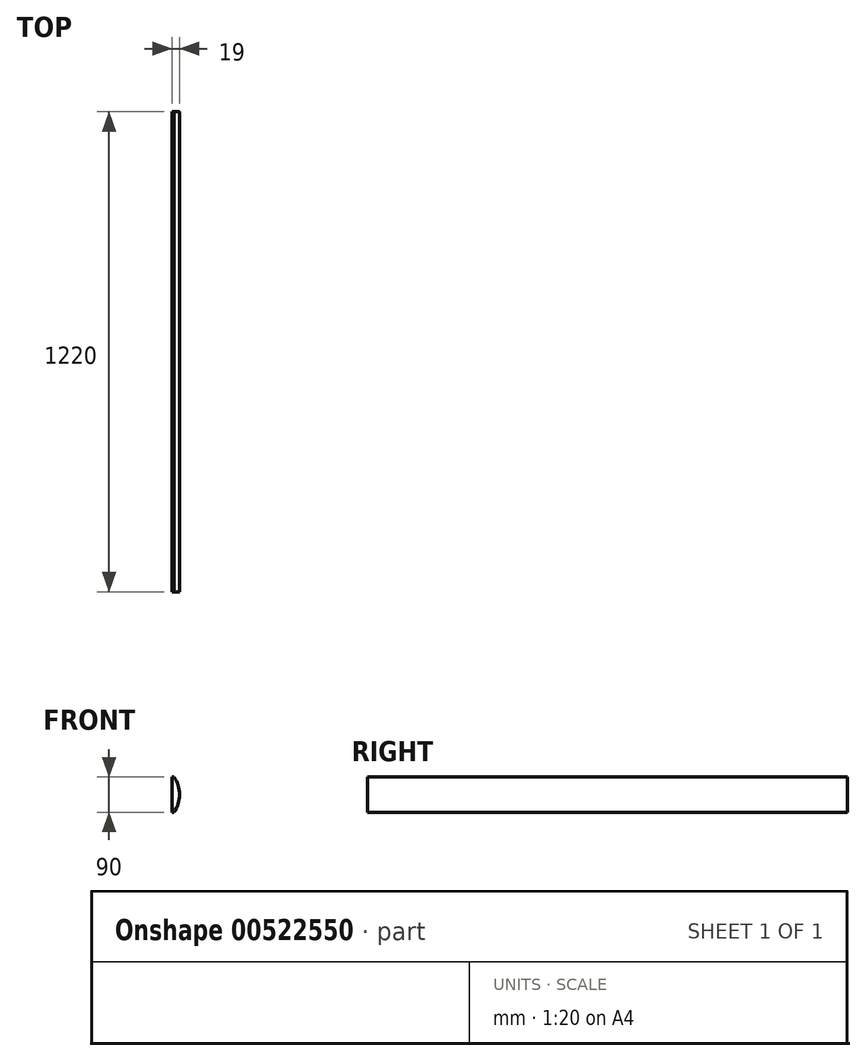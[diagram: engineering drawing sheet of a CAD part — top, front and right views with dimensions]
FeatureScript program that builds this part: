
annotation { "Feature Type Name" : "Feature", "Feature Type Description" : "" }
export const myFeature = defineFeature(function(context is Context, id is Id, definition is map)
    precondition{}
    {
        {
            var Q0;
            Q0=qCreatedBy(makeId("Front.planeOp"),FACE);
            var sketch = newSketch(context, id + "F0", { "sketchPlane" : qUnion([Q0])});
            skLineSegment(sketch, "E0", {"start": v(0, 0) * mm, "end": v(0, 90) * mm});
            skLineSegment(sketch, "E1", {"start": v(0, 0) * mm, "end": v(5, 0) * mm});
            skLineSegment(sketch, "E2", {"start": v(0, 90) * mm, "end": v(5, 90) * mm});
            skLineSegment(sketch, "E3", {"start": v(0, 45) * mm, "end": v(19, 45) * mm});
            skPoint(sketch, "E3.endSnap0", {"position": v(0, 45) * mm});
            skArc(sketch, "E4", {"start": v(5, 0) * mm, "mid": v(19, 45) * mm, "end": v(5, 90) * mm});
            skSolve(sketch);
        }
        {
            var Q0;
            Q0=qSketchRegion(id+"F0",true);
            extrude(context, id + "F1", {"entities" : qUnion([Q0]), "depth" : 1220 * mm, "offsetDistance" : 25 * mm});
        }
    });
